FCSTD DOCUMENT  (FreeCAD 0.18R13588 (Git))
Label: sod-70_P5.08mm
License: All rights reserved
LicenseURL: http://en.wikipedia.org/wiki/All_rights_reserved
objects: Sketcher::SketchObject×4, App::Annotation×2, App::DocumentObjectGroup×1, Spreadsheet::Sheet×1
note: 4 computed .brp shape members not serialized (recipe doc carries the construction recipe); baked Part::Feature solids carry a one-line shape summary decoded from their .brp

FEATURE [Sketcher::SketchObject] Sketch  label="F_Fab_0.1"
  expr: Constraints[5] = Spreadsheet.pitch / 2
  expr: Constraints[3] = 4.5999999999999996 / 2
  sketch-geometry (2):
    g0: ArcOfCircle CenterX=2.54 CenterY=0 CenterZ=0 NormalX=0 NormalY=0 NormalZ=1 AngleXU=0 Radius=2.3 StartAngle=5.54369 EndAngle=10.1643
    g1: LineSegment StartX=4.23926 StartY=-1.55 StartZ=0 EndX=0.840735 EndY=-1.55 EndZ=0
  constraints (7):
    c: Horizontal(g1)
    c: Coincident(g0,g1)
    c: Coincident(g0,g1)
    c: Radius(g0) = 2.3
    c: DistanceY(g0,g-1) = 1.55
    c: DistanceX(g-1,g0) = 2.54
    c: PointOnObject(g0,g-1)
FEATURE [App::Annotation] Text  label="Ref#_1.00mm"
  LabelText = Ref
  Position = (0,4.5,0)
FEATURE [App::Annotation] Text001  label="Value#_1.00mm"
  LabelText = SOD-70_P5.08mm 
  Position = (0,-6,0)
FEATURE [Sketcher::SketchObject] Sketch001  label="Pads_TH_SMD"
  expr: Constraints[31] = Spreadsheet.pitch
  sketch-geometry (14):
    g0: LineSegment StartX=-0.6 StartY=0.85 StartZ=0 EndX=0.6 EndY=0.85 EndZ=0
    g1: LineSegment StartX=0.6 StartY=0.85 StartZ=0 EndX=0.6 EndY=-0.85 EndZ=0
    g2: LineSegment StartX=0.6 StartY=-0.85 StartZ=0 EndX=-0.6 EndY=-0.85 EndZ=0
    g3: LineSegment StartX=-0.6 StartY=-0.85 StartZ=0 EndX=-0.6 EndY=0.85 EndZ=0
    g4: ArcOfCircle CenterX=5.08 CenterY=0.25 CenterZ=0 NormalX=0 NormalY=0 NormalZ=1 AngleXU=0 Radius=0.6 StartAngle=0 EndAngle=3.14159
    g5: ArcOfCircle CenterX=5.08 CenterY=-0.25 CenterZ=0 NormalX=0 NormalY=0 NormalZ=1 AngleXU=0 Radius=0.6 StartAngle=3.14159 EndAngle=6.28319
    g6: LineSegment StartX=4.48 StartY=0.25 StartZ=0 EndX=4.48 EndY=-0.25 EndZ=0
    g7: LineSegment StartX=5.68 StartY=0.25 StartZ=0 EndX=5.68 EndY=-0.25 EndZ=0
    g8: LineSegment [constr] StartX=5.08 StartY=0.85 StartZ=0 EndX=5.08 EndY=-0.85 EndZ=0
    g9: Circle CenterX=0 CenterY=0 CenterZ=0 NormalX=0 NormalY=0 NormalZ=1 AngleXU=0 Radius=0.35
    g10: Circle CenterX=5.08 CenterY=0 CenterZ=0 NormalX=0 NormalY=0 NormalZ=1 AngleXU=0 Radius=0.35
    g11: LineSegment [constr] StartX=4.48 StartY=0.25 StartZ=0 EndX=5.68 EndY=0.25 EndZ=0
    g12: GeomPoint X=0 Y=0.35 Z=0
    g13: GeomPoint X=0.35 Y=0 Z=0
  constraints (36):
    c: Coincident(g1,g2)
    c: Coincident(g2,g3)
    c: Coincident(g3,g0)
    c: Horizontal(g0)
    c: Horizontal(g2)
    c: Vertical(g1)
    c: Vertical(g3)
    c: Tangent(g4,g7) = 1.5708
    c: Tangent(g4,g6) = -1.5708
    c: Tangent(g6,g5) = -1.5708
    c: Tangent(g7,g5) = 1.5708
    c: Equal(g4,g5)
    c: Symmetric(g4,g5,g-1)
    c: Symmetric(g0,g1,g-1)
    c: PointOnObject(g8,g4)
    c: PointOnObject(g8,g5)
    c: Vertical(g8)
    c: PointOnObject(g4,g8)
    c: PointOnObject(g10,g8)
    c: PointOnObject(g10,g-1)
    c: Radius(g9) = 0.35
    c: Equal(g9,g10)
    c: Coincident(g11,g4)
    c: Coincident(g11,g4)
    c: Equal(g11,g0)
    c: PointOnObject(g12,g9)
    c: DistanceY(g12,g0) = 0.5
    c: Coincident(g9,g-1)
    c: PointOnObject(g12,g-2)
    c: Symmetric(g0,g0,g-2)
    c: Equal(g1,g8)
    c: DistanceX(g-1,g8) = 5.08
    c: PointOnObject(g13,g9)
    c: PointOnObject(g13,g-1)
    c: DistanceX(g13,g0) = 0.25
    c: Coincident(g1,g0)
FEATURE [Sketcher::SketchObject] Sketch002  label="F_Silks_0.12"
  ExternalGeometry = -> [Sketch,Sketch001]
  sketch-geometry (9):
    g0: ArcOfCircle [constr] CenterX=2.54 CenterY=0 CenterZ=0 NormalX=0 NormalY=0 NormalZ=1 AngleXU=0 Radius=2.41 StartAngle=5.52336 EndAngle=10.1846
    g1: LineSegment StartX=4.28714 StartY=-1.66 StartZ=0 EndX=0.792859 EndY=-1.66 EndZ=0
    g2: GeomPoint X=4.84 Y=0 Z=0
    g3: GeomPoint X=4.95 Y=0 Z=0
    g4: ArcOfCircle CenterX=2.54 CenterY=0 CenterZ=0 NormalX=0 NormalY=0 NormalZ=1 AngleXU=0 Radius=2.41 StartAngle=0.416689 EndAngle=2.69079
    g5: GeomPoint X=4.81707 Y=0.789324 Z=0
    g6: GeomPoint X=4.81707 Y=-0.789324 Z=0
    g7: ArcOfCircle CenterX=2.54 CenterY=0 CenterZ=0 NormalX=0 NormalY=0 NormalZ=1 AngleXU=0 Radius=2.41 StartAngle=5.52336 EndAngle=5.8665
    g8: ArcOfCircle CenterX=2.54 CenterY=0 CenterZ=0 NormalX=0 NormalY=0 NormalZ=1 AngleXU=0 Radius=2.41 StartAngle=3.59239 EndAngle=3.90142
  constraints (24):
    c: Horizontal(g1)
    c: Coincident(g0,g1)
    c: Coincident(g0,g1)
    c: Coincident(g0,g-3)
    c: PointOnObject(g2,g-3)
    c: PointOnObject(g3,g0)
    c: PointOnObject(g3,g-1)
    c: PointOnObject(g2,g-1)
    c: DistanceX(g2,g3) = 0.11
    c: DistanceY(g0,g-3) = 0.11
    c: Equal(g4,g0)
    c: DistanceY(g-4,g4) = 0.2
    c: Coincident(g4,g0)
    c: PointOnObject(g5,g-5)
    c: PointOnObject(g5,g0)
    c: PointOnObject(g6,g-6)
    c: PointOnObject(g6,g0)
    c: Coincident(g7,g0)
    c: Coincident(g7,g0)
    c: Distance(g7,g6) = 0.2
    c: Distance(g5,g4) = 0.2
    c: Coincident(g8,g0)
    c: Coincident(g8,g0)
    c: DistanceY(g8,g-7) = 0.2
FEATURE [Sketcher::SketchObject] Sketch003  label="F_CrtYd_0.05"
  ExternalGeometry = -> [Sketch,Sketch001]
  sketch-geometry (22):
    g0: LineSegment [constr] StartX=0.24 StartY=0 StartZ=0 EndX=4.84 EndY=0 EndZ=0
    g1: LineSegment [constr] StartX=2.54 StartY=0 StartZ=0 EndX=2.54 EndY=2.3 EndZ=0
    g2: LineSegment StartX=1.48376 StartY=2.55 StartZ=0 EndX=3.59624 EndY=2.55 EndZ=0
    g3: LineSegment [constr] StartX=5.09 StartY=1.05624 StartZ=0 EndX=5.09 EndY=-1.05624 EndZ=0
    g4: LineSegment StartX=4.34624 StartY=-1.8 StartZ=0 EndX=0.733755 EndY=-1.8 EndZ=0
    g5: LineSegment [constr] StartX=-0.01 StartY=-1.05624 StartZ=0 EndX=-0.01 EndY=1.05624 EndZ=0
    g6: LineSegment [constr] StartX=2.54 StartY=0 StartZ=0 EndX=0.913654 EndY=1.62635 EndZ=0
    g7: LineSegment [constr] StartX=1.48376 StartY=2.55 StartZ=0 EndX=-0.01 EndY=1.05624 EndZ=0
    g8: LineSegment [constr] StartX=3.59624 StartY=2.55 StartZ=0 EndX=5.09 EndY=1.05624 EndZ=0
    g9: GeomPoint X=0.736878 Y=1.80312 Z=0
    g10: LineSegment [constr] StartX=-0.01 StartY=-1.05624 StartZ=0 EndX=0.733755 EndY=-1.8 EndZ=0
    g11: LineSegment [constr] StartX=4.34624 StartY=-1.8 StartZ=0 EndX=5.09 EndY=-1.05624 EndZ=0
    g12: LineSegment StartX=1.48376 StartY=2.55 StartZ=0 EndX=0.0337554 EndY=1.1 EndZ=0
    g13: LineSegment StartX=0.0337554 StartY=1.1 StartZ=0 EndX=-0.85 EndY=1.1 EndZ=0
    g14: LineSegment StartX=-0.85 StartY=1.1 StartZ=0 EndX=-0.85 EndY=-1.1 EndZ=0
    g15: LineSegment StartX=-0.85 StartY=-1.1 StartZ=0 EndX=0.0337554 EndY=-1.1 EndZ=0
    g16: LineSegment StartX=0.0337554 StartY=-1.1 StartZ=0 EndX=0.733755 EndY=-1.8 EndZ=0
    g17: LineSegment StartX=3.59624 StartY=2.55 StartZ=0 EndX=5.04624 EndY=1.1 EndZ=0
    g18: LineSegment StartX=5.04624 StartY=1.1 StartZ=0 EndX=5.93 EndY=1.1 EndZ=0
    g19: LineSegment StartX=5.93 StartY=1.1 StartZ=0 EndX=5.93 EndY=-1.1 EndZ=0
    g20: LineSegment StartX=5.93 StartY=-1.1 StartZ=0 EndX=5.04624 EndY=-1.1 EndZ=0
    g21: LineSegment StartX=5.04624 StartY=-1.1 StartZ=0 EndX=4.34624 EndY=-1.8 EndZ=0
  constraints (64):
    c: PointOnObject(g0,g-3)
    c: PointOnObject(g0,g-3)
    c: Horizontal(g0)
    c: Coincident(g1,g-3)
    c: PointOnObject(g1,g-3)
    c: PointOnObject(g0,g-1)
    c: Horizontal(g2)
    c: Horizontal(g4)
    c: Vertical(g3)
    c: Vertical(g5)
    c: Coincident(g6,g1)
    c: PointOnObject(g6,g-3)
    c: Angle(g1,g6) = 0.785398
    c: Perpendicular(g6,g7)
    c: Perpendicular(g7,g8)
    c: Equal(g8,g7)
    c: Coincident(g2,g7)
    c: Coincident(g5,g7)
    c: Coincident(g2,g8)
    c: Coincident(g3,g8)
    c: DistanceX(g0,g3) = 0.25
    c: DistanceX(g5,g0) = 0.25
    c: DistanceY(g1,g2) = 0.25
    c: PointOnObject(g9,g7)
    c: PointOnObject(g9,g6)
    c: Vertical(g1)
    c: Equal(g2,g7)
    c: Distance(g9,g6) = 0.25
    c: Perpendicular(g7,g10)
    c: Coincident(g5,g10)
    c: Coincident(g4,g10)
    c: Coincident(g4,g11)
    c: Coincident(g3,g11)
    c: Perpendicular(g10,g11)
    c: Equal(g5,g3)
    c: Equal(g3,g7)
    c: DistanceY(g4,g-3) = 0.25
    c: Coincident(g2,g12)
    c: PointOnObject(g12,g7)
    c: Coincident(g12,g13)
    c: Horizontal(g13)
    c: Coincident(g13,g14)
    c: Vertical(g14)
    c: Coincident(g14,g15)
    c: Horizontal(g15)
    c: Coincident(g15,g16)
    c: Coincident(g16,g4)
    c: PointOnObject(g15,g10)
    c: DistanceY(g-4,g12) = 0.25
    c: DistanceX(g13,g-4) = 0.25
    c: DistanceY(g14,g-5) = 0.25
    c: Coincident(g2,g17)
    c: PointOnObject(g17,g8)
    c: Coincident(g17,g18)
    c: Horizontal(g18)
    c: Coincident(g18,g19)
    c: Vertical(g19)
    c: Coincident(g19,g20)
    c: PointOnObject(g20,g11)
    c: Horizontal(g20)
    c: Coincident(g20,g21)
    c: Coincident(g21,g4)
    c: PointOnObject(g19,g15)
    c: Symmetric(g18,g13,g1)
FEATURE [App::DocumentObjectGroup] Group  label="SOD-70_P5.08mm"
  Group = -> [Text,Text001,Sketch,Sketch001,Sketch002,Sketch003]
FEATURE [Spreadsheet::Sheet] Spreadsheet
  cells = A1=pitch; B1(pitch)=5.0800000000000001
